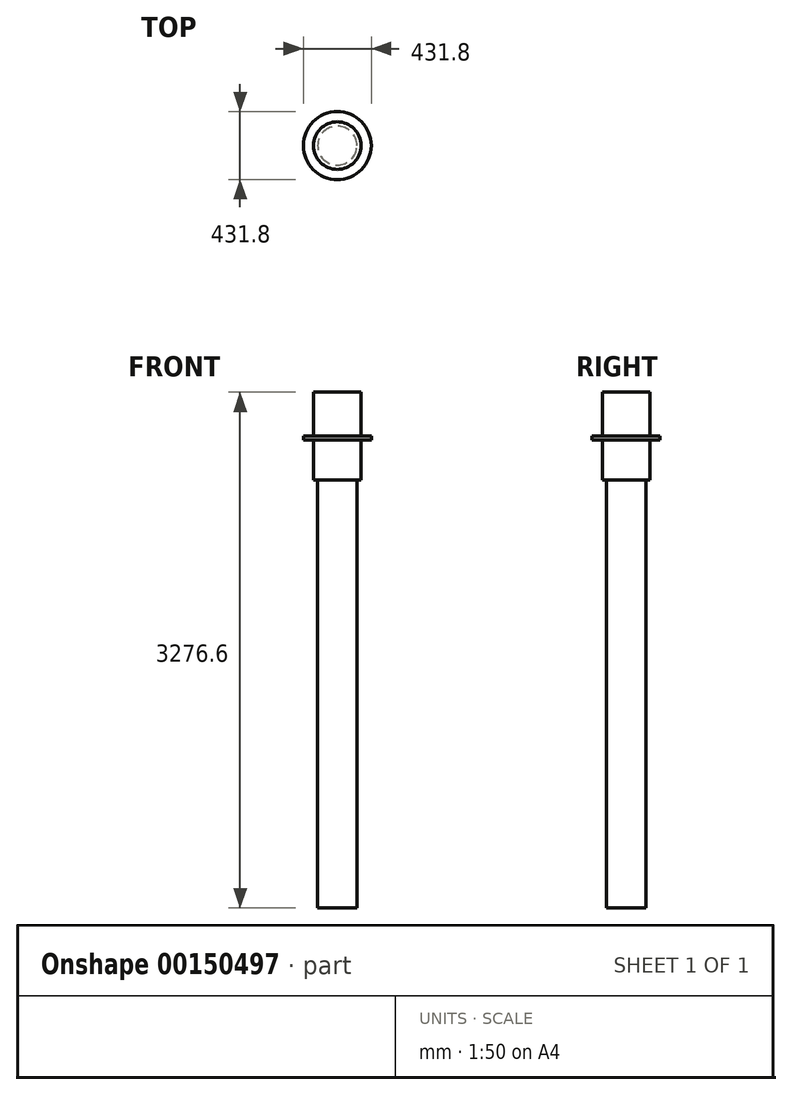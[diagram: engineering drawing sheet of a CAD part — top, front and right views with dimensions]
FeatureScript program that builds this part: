
annotation { "Feature Type Name" : "Feature", "Feature Type Description" : "" }
export const myFeature = defineFeature(function(context is Context, id is Id, definition is map)
    precondition{}
    {
        {
            var Q0;
            Q0=qCreatedBy(makeId("Top.planeOp"),FACE);
            var sketch = newSketch(context, id + "F0", { "sketchPlane" : qUnion([Q0])});
            skCircle(sketch, "E0", {"center": v(0, 0) * mm, "radius": 124.46 * mm});
            skSolve(sketch);
        }
        {
            var Q0;
            Q0=makeQuery(id+"F0.imprint","IMPRINT",FACE,{"disambiguationData":[TD([[makeQuery(id+"F0.imprint","IMPRINT",EDGE,{"derivedFrom":sQuery(id+"F0.wireOp",EDGE,"E0")}),1.0]])]});
            extrude(context, id + "F1", {"entities" : qUnion([Q0]), "oppositeDirection" : true, "depth" : 2717.8 * mm});
        }
        {
            var Q0;
            Q0=qCreatedBy(makeId("Top.planeOp"),FACE);
            var sketch = newSketch(context, id + "F2", { "sketchPlane" : qUnion([Q0])});
            skCircle(sketch, "E1", {"center": v(0, 0) * mm, "radius": 151.13 * mm});
            skSolve(sketch);
        }
        {
            var Q0;
            Q0=makeQuery(id+"F2.imprint","IMPRINT",FACE,{"disambiguationData":[TD([[makeQuery(id+"F2.imprint","IMPRINT",EDGE,{"derivedFrom":sQuery(id+"F2.wireOp",EDGE,"E1")}),1.0]])]});
            extrude(context, id + "F3", {"entities" : qUnion([Q0]), "operationType" : NewBodyOperationType.ADD, "depth" : 254 * mm});
        }
        {
            var Q0;
            Q0=makeQuery(id+"F3.opExtrude","CAP_FACE",FACE,{"disambiguationData":[OSD([sQuery(id+"F2.wireOp",EDGE,"E1")])],"isStart":false});
            var sketch = newSketch(context, id + "F4", { "sketchPlane" : qUnion([Q0])});
            skCircle(sketch, "E2", {"center": v(0, 0) * mm, "radius": 215.9 * mm});
            skSolve(sketch);
        }
        {
            var Q0;
            Q0=makeQuery(id+"F4.imprint","IMPRINT",FACE,{"disambiguationData":[TD([[makeQuery(id+"F4.imprint","IMPRINT",EDGE,{"derivedFrom":sQuery(id+"F4.wireOp",EDGE,"E2")}),1.0]])]});
            var Q1;
            Q1=makeQuery(id+"F4.imprint","IMPRINT",FACE,{"disambiguationData":[TD([[makeQuery(id+"F4.imprint","IMPRINT",EDGE,{"derivedFrom":makeQuery(id+"F3.opExtrude","CAP_EDGE",EDGE,{"disambiguationData":[OSD([sQuery(id+"F2.wireOp",EDGE,"E1")])],"isStart":false})}),1.0]])]});
            extrude(context, id + "F5", {"entities" : qUnion([Q0, Q1]), "depth" : 25.4 * mm});
        }
        {
            var Q0;
            Q0=makeQuery(id+"F5.opExtrude","CAP_FACE",FACE,{"disambiguationData":[OSD([sQuery(id+"F4.wireOp",EDGE,"E2")])],"isStart":false});
            var sketch = newSketch(context, id + "F6", { "sketchPlane" : qUnion([Q0])});
            skCircle(sketch, "E3", {"center": v(0, 0) * mm, "radius": 151.13 * mm});
            skSolve(sketch);
        }
        {
            var Q0;
            Q0=makeQuery(id+"F6.imprint","IMPRINT",FACE,{"disambiguationData":[TD([[makeQuery(id+"F6.imprint","IMPRINT",EDGE,{"derivedFrom":sQuery(id+"F6.wireOp",EDGE,"E3")}),1.0]])]});
            extrude(context, id + "F7", {"entities" : qUnion([Q0]), "operationType" : NewBodyOperationType.ADD, "depth" : 279.4 * mm});
        }
    });
